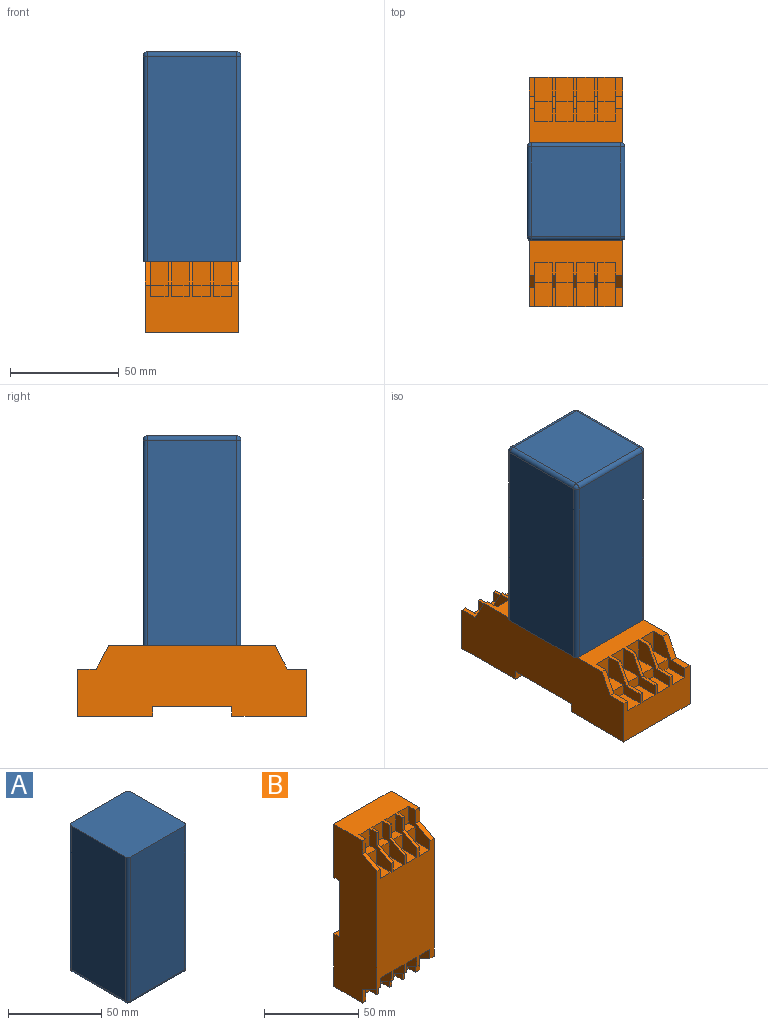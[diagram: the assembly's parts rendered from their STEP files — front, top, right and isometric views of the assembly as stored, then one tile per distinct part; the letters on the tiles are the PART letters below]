
ASSEMBLY  parts=2 mates=1
PART A: 18 faces, bbox 45x45x96.5 mm
  f0: sphere r=2mm, area 5.4mm2, adj f2,f7,f8
  f1: sphere r=2mm, area 5.4mm2, adj f4,f8,f9
  f2: cylinder r=2mm len=94.5mm, axis (0,0,1), area 296.9mm2, adj f0,f3,f6,f11
  f3: plane 94.5x41mm, normal (0,1,0), area 3874.5mm2, adj f2,f4,f8,f11
  f4: cylinder r=2mm len=94.5mm, axis (0,0,1), area 296.9mm2, adj f1,f3,f5,f11
  f5: plane 94.5x41mm, normal (1,0,0), area 3874.5mm2, adj f4,f9,f10,f11
  f6: plane 94.5x41mm, normal (-1,0,0), area 3874.5mm2, adj f2,f7,f11,f12
  f7: cylinder r=2mm len=41mm, axis (0,-1,0), area 128.8mm2, adj f0,f6,f13,f14
  f8: cylinder r=2mm len=41mm, axis (-1,0,0), area 128.8mm2, adj f0,f1,f3,f14
  f9: cylinder r=2mm len=41mm, axis (0,1,0), area 128.8mm2, adj f1,f5,f14,f15
  f10: cylinder r=2mm len=94.5mm, axis (0,0,1), area 296.9mm2, adj f5,f11,f15,f16
  f11: plane 45x45mm, normal (0,0,1), area 2021.6mm2, adj f2,f3,f4,f5,f6,f10,f12,f16
  f12: cylinder r=2mm len=94.5mm, axis (0,0,1), area 296.9mm2, adj f6,f11,f13,f16
  f13: sphere r=2mm, area 5.4mm2, adj f7,f12,f17
  f14: plane 41x41mm, normal (0,0,-1), area 1681mm2, adj f7,f8,f9,f17
  f15: sphere r=2mm, area 5.4mm2, adj f9,f10,f17
  f16: plane 94.5x41mm, normal (0,-1,0), area 3874.5mm2, adj f10,f11,f12,f17
  f17: cylinder r=2mm len=41mm, axis (1,0,0), area 128.8mm2, adj f13,f14,f15,f16
PART B: 78 faces, bbox 43x32.4x105.3 mm
  f0: plane 8.11x5mm, normal (0,0,-1), area 40.6mm2, adj f1,f32,f38,f40
  f1: plane 9.4x8.11mm, normal (0,-1,0), area 76.3mm2, adj f0,f38,f39,f40
  f2: plane 8.64x3.33mm, normal (0,-1,0), area 28.7mm2, adj f23,f42,f43,f44
  f3: plane 10.93x8.11mm, normal (0,-1,0), area 88.7mm2, adj f4,f23,f44,f46
  f4: plane 8.11x5mm, normal (0,0,1), area 40.6mm2, adj f3,f5,f44,f46
  f5: plane 9.4x8.11mm, normal (0,-1,0), area 76.3mm2, adj f4,f44,f45,f46
  f6: plane 8.64x1.59mm, normal (0,-1,0), area 13.7mm2, adj f23,f46,f47,f48
  f7: plane 10.93x8.11mm, normal (0,-1,0), area 88.7mm2, adj f8,f23,f48,f50
  f8: plane 8.11x5mm, normal (0,0,1), area 40.6mm2, adj f7,f9,f48,f50
  f9: plane 9.4x8.11mm, normal (0,-1,0), area 76.3mm2, adj f8,f48,f49,f50
  f10: plane 8.64x1.59mm, normal (0,-1,0), area 13.7mm2, adj f23,f50,f51,f52
  f11: plane 10.93x8.11mm, normal (0,-1,0), area 88.7mm2, adj f12,f23,f52,f54
  f12: plane 8.11x5mm, normal (0,0,1), area 40.6mm2, adj f11,f13,f52,f54
  f13: plane 9.4x8.11mm, normal (0,-1,0), area 76.3mm2, adj f12,f52,f53,f54
  f14: plane 8.64x1.59mm, normal (0,-1,0), area 13.7mm2, adj f23,f54,f55,f56
  f15: plane 10.93x8.11mm, normal (0,-1,0), area 88.7mm2, adj f16,f23,f56,f58
  f16: plane 8.11x5mm, normal (0,0,1), area 40.6mm2, adj f15,f17,f56,f58
  f17: plane 9.4x8.11mm, normal (0,-1,0), area 76.3mm2, adj f16,f56,f57,f58
  f18: plane 8.64x2.46mm, normal (0,-1,0), area 21.3mm2, adj f23,f58,f59,f60
  f19: plane 43x4.39mm, normal (0,0,1), area 188.7mm2, adj f20,f30,f42,f60
  f20: plane 43x36.45mm, normal (0,1,0), area 1567.3mm2, adj f19,f21,f42,f60
  f21: plane 43x4.39mm, normal (0,0,-1), area 188.7mm2, adj f20,f22,f42,f60
  f22: plane 43x34.55mm, normal (0,1,0), area 1485.5mm2, adj f21,f23,f42,f60
  f23: plane 43x21.67mm, normal (0,0,1), area 762.1mm2, adj f2,f3,f6,f7,f10,f11,f14,f15
  f24: plane 8.11x5mm, normal (0,0,-1), area 40.6mm2, adj f25,f28,f62,f64
  f25: plane 9.4x8.11mm, normal (0,-1,0), area 76.3mm2, adj f24,f62,f63,f64
  f26: plane 9.4x8.11mm, normal (0,-1,0), area 76.3mm2, adj f27,f35,f36,f65
  f27: plane 8.11x5mm, normal (0,0,-1), area 40.6mm2, adj f26,f34,f36,f65
  f28: plane 10.93x8.11mm, normal (0,-1,0), area 88.7mm2, adj f24,f62,f64,f68
  f29: plane 8.91x2.46mm, normal (0,-1,0), area 21.9mm2, adj f60,f61,f62,f68
  f30: plane 43x34.3mm, normal (0,1,0), area 1474.9mm2, adj f19,f42,f60,f68
  f31: plane 8.91x3.33mm, normal (0,-1,0), area 29.6mm2, adj f40,f41,f42,f68
  f32: plane 10.93x8.11mm, normal (0,-1,0), area 88.7mm2, adj f0,f38,f40,f68
  f33: plane 8.91x1.59mm, normal (0,-1,0), area 14.1mm2, adj f36,f37,f38,f68
  f34: plane 10.93x8.11mm, normal (0,-1,0), area 88.7mm2, adj f27,f36,f65,f68
  f35: plane 11x8.11mm, normal (0,0,-1), area 89.2mm2, adj f26,f36,f65,f69
  f36: plane 20.33x16mm, normal (-1,0,0), area 153mm2, adj f26,f27,f33,f34,f35,f37,f68,f69
  f37: plane 10.77x5.45mm, normal (0,-0.45,-0.89), area 19.2mm2, adj f33,f36,f38,f69
  f38: plane 20.33x16mm, normal (1,0,0), area 153mm2, adj f0,f1,f32,f33,f37,f39,f68,f69
  f39: plane 11x8.11mm, normal (0,0,-1), area 89.2mm2, adj f1,f38,f40,f69
  f40: plane 20.33x16mm, normal (-1,0,0), area 153mm2, adj f0,f1,f31,f32,f39,f41,f68,f69
  f41: plane 10.77x5.45mm, normal (0,-0.45,-0.89), area 40.1mm2, adj f31,f40,f42,f69
  f42: plane 105.3x32.44mm, normal (1,0,0), area 3006.7mm2, adj f2,f19,f20,f21,f22,f23,f30,f31
  f43: plane 10.77x5.72mm, normal (0,-0.47,0.88), area 40.5mm2, adj f2,f42,f44,f69
  f44: plane 20.33x16mm, normal (-1,0,0), area 154.5mm2, adj f2,f3,f4,f5,f23,f43,f45,f69
  f45: plane 11x8.11mm, normal (0,0,1), area 89.2mm2, adj f5,f44,f46,f69
  f46: plane 20.33x16mm, normal (1,0,0), area 154.5mm2, adj f3,f4,f5,f6,f23,f45,f47,f69
  f47: plane 10.77x5.72mm, normal (0,-0.47,0.88), area 19.4mm2, adj f6,f46,f48,f69
  f48: plane 20.33x16mm, normal (-1,0,0), area 154.5mm2, adj f6,f7,f8,f9,f23,f47,f49,f69
  f49: plane 11x8.11mm, normal (0,0,1), area 89.2mm2, adj f9,f48,f50,f69
  f50: plane 20.33x16mm, normal (1,0,0), area 154.5mm2, adj f7,f8,f9,f10,f23,f49,f51,f69
  f51: plane 10.77x5.72mm, normal (0,-0.47,0.88), area 19.4mm2, adj f10,f50,f52,f69
  f52: plane 20.33x16mm, normal (-1,0,0), area 154.5mm2, adj f10,f11,f12,f13,f23,f51,f53,f69
  f53: plane 11x8.11mm, normal (0,0,1), area 89.2mm2, adj f13,f52,f54,f69
  f54: plane 20.33x16mm, normal (1,0,0), area 154.5mm2, adj f11,f12,f13,f14,f23,f53,f55,f69
  f55: plane 10.77x5.72mm, normal (0,-0.47,0.88), area 19.4mm2, adj f14,f54,f56,f69
  f56: plane 20.33x16mm, normal (-1,0,0), area 154.5mm2, adj f14,f15,f16,f17,f23,f55,f57,f69
  f57: plane 11x8.11mm, normal (0,0,1), area 89.2mm2, adj f17,f56,f58,f69
  f58: plane 20.33x16mm, normal (1,0,0), area 154.5mm2, adj f15,f16,f17,f18,f23,f57,f59,f69
  f59: plane 10.77x5.72mm, normal (0,-0.47,0.88), area 30mm2, adj f18,f58,f60,f69
  f60: plane 105.3x32.44mm, normal (-1,0,0), area 3006.7mm2, adj f18,f19,f20,f21,f22,f23,f29,f30
  f61: plane 10.77x5.45mm, normal (0,-0.45,-0.89), area 29.7mm2, adj f29,f60,f62,f69
  f62: plane 20.33x16mm, normal (1,0,0), area 153mm2, adj f24,f25,f28,f29,f61,f63,f68,f69
  f63: plane 11x8.11mm, normal (0,0,-1), area 89.2mm2, adj f25,f62,f64,f69
  f64: plane 20.33x16mm, normal (-1,0,0), area 153mm2, adj f24,f25,f28,f63,f66,f67,f68,f69
  f65: plane 20.33x16mm, normal (1,0,0), area 153mm2, adj f26,f27,f34,f35,f68,f69,f70,f71
  f66: plane 8.91x1.59mm, normal (0,-1,0), area 14.1mm2, adj f64,f67,f68,f73
  f67: plane 10.77x5.45mm, normal (0,-0.45,-0.89), area 19.2mm2, adj f64,f66,f69,f73
  f68: plane 43x21.67mm, normal (0,0,-1), area 762.1mm2, adj f28,f29,f30,f31,f32,f33,f34,f36
  f69: plane 76.58x43mm, normal (0,-1,0), area 2905.3mm2, adj f35,f36,f37,f38,f39,f40,f41,f42
  f70: plane 10.77x5.45mm, normal (0,-0.45,-0.89), area 19.2mm2, adj f65,f69,f71,f75
  f71: plane 8.91x1.59mm, normal (0,-1,0), area 14.1mm2, adj f65,f68,f70,f75
  f72: plane 10.93x8.11mm, normal (0,-1,0), area 88.7mm2, adj f68,f73,f75,f76
  f73: plane 20.33x16mm, normal (1,0,0), area 153mm2, adj f66,f67,f68,f69,f72,f74,f76,f77
  f74: plane 11x8.11mm, normal (0,0,-1), area 89.2mm2, adj f69,f73,f75,f77
  f75: plane 20.33x16mm, normal (-1,0,0), area 153mm2, adj f68,f69,f70,f71,f72,f74,f76,f77
  f76: plane 8.11x5mm, normal (0,0,-1), area 40.6mm2, adj f72,f73,f75,f77
  f77: plane 9.4x8.11mm, normal (0,-1,0), area 76.3mm2, adj f73,f74,f75,f76
PLACE A rot(axis=(1,0,0),180deg) t=(62.18,41.1,124.55)mm
PLACE B rot(axis=(-1,0,0),90deg) t=(-21.5,-95.24,5.75)mm fixed
MATE fastened B.f69 <-> A.f11  axis (0,0,1) through (0.06,0.12,28.05)mm
